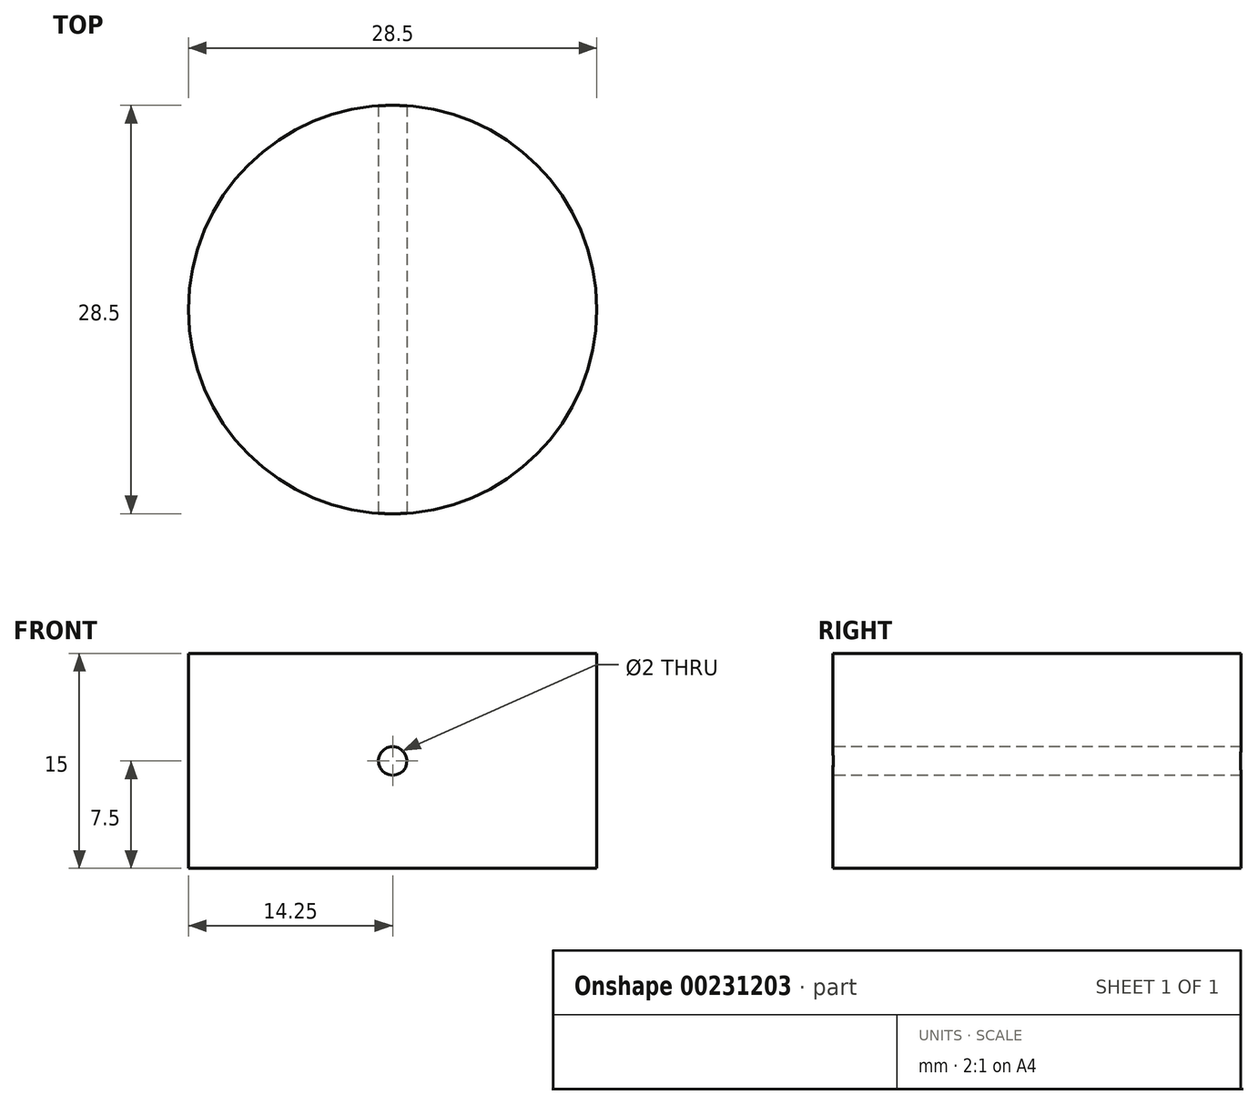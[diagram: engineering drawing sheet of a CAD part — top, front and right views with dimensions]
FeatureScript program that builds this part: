
annotation { "Feature Type Name" : "Feature", "Feature Type Description" : "" }
export const myFeature = defineFeature(function(context is Context, id is Id, definition is map)
    precondition{}
    {
        {
            var Q0;
            Q0=qCreatedBy(makeId("Top.planeOp"),FACE);
            var sketch = newSketch(context, id + "F0", { "sketchPlane" : qUnion([Q0])});
            skCircle(sketch, "E0", {"center": v(0, 0) * mm, "radius": 14.25 * mm});
            skSolve(sketch);
        }
        {
            var Q0;
            Q0=makeQuery(id+"F0.imprint","IMPRINT",FACE,{"disambiguationData":[TD([[makeQuery(id+"F0.imprint","IMPRINT",EDGE,{"derivedFrom":sQuery(id+"F0.wireOp",EDGE,"E0")}),1.0]])]});
            extrude(context, id + "F1", {"entities" : qUnion([Q0]), "depth" : 15 * mm});
        }
        {
            var Q0;
            Q0=qCreatedBy(makeId("Front.planeOp"),FACE);
            cPlane(context, id + "F2", {"entities" : qUnion([Q0]), "cplaneType" : CPlaneType.OFFSET, "offset" : 14.25 * mm, "width" : 150 * mm, "height" : 150 * mm});
        }
        {
            var Q0;
            Q0=qCreatedBy(id+"F2.planeOp",FACE);
            var sketch = newSketch(context, id + "F3", { "sketchPlane" : qUnion([Q0])});
            skCircle(sketch, "E1", {"center": v(0, 7.5) * mm, "radius": 1 * mm});
            skSolve(sketch);
        }
        {
            var Q0;
            Q0=makeQuery(id+"F3.imprint","IMPRINT",FACE,{"disambiguationData":[TD([[makeQuery(id+"F3.imprint","IMPRINT",EDGE,{"derivedFrom":sQuery(id+"F3.wireOp",EDGE,"E1")}),1.0]])]});
            extrude(context, id + "F4", {"entities" : qUnion([Q0]), "operationType" : NewBodyOperationType.REMOVE, "oppositeDirection" : true, "depth" : 28.5 * mm});
        }
    });
